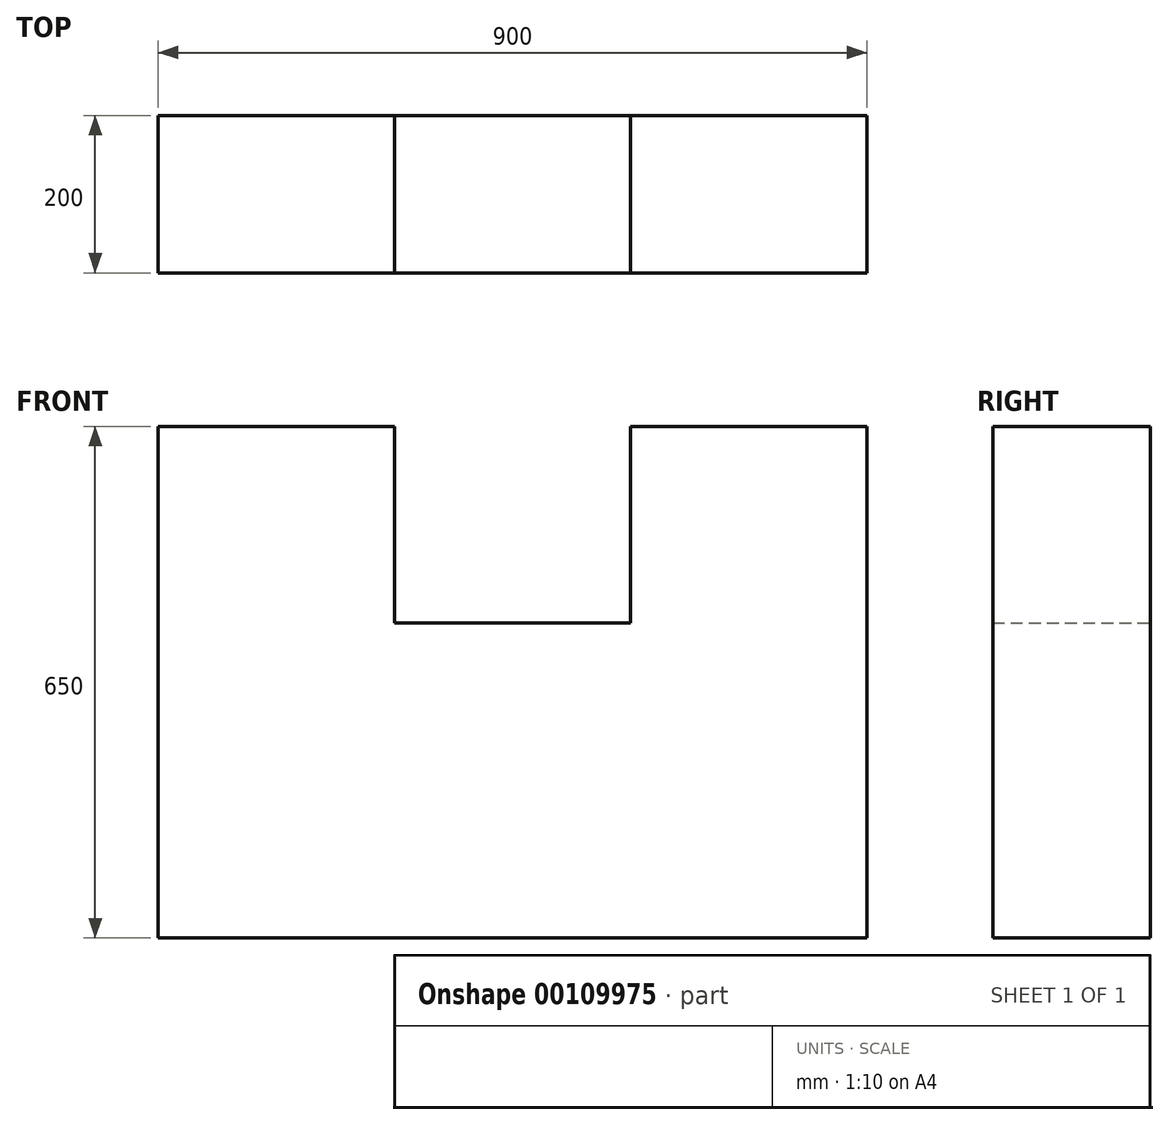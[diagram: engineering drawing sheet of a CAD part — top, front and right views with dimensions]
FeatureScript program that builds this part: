
annotation { "Feature Type Name" : "Feature", "Feature Type Description" : "" }
export const myFeature = defineFeature(function(context is Context, id is Id, definition is map)
    precondition{}
    {
        {
            var Q0;
            Q0=qCreatedBy(makeId("Front.planeOp"),FACE);
            var sketch = newSketch(context, id + "F0", { "sketchPlane" : qUnion([Q0])});
            skLineSegment(sketch, "E0.bottom", {"start": v(450, -325) * mm, "end": v(-450, -325) * mm});
            skLineSegment(sketch, "E0.top", {"start": v(450, 325) * mm, "end": v(-450, 325) * mm});
            skLineSegment(sketch, "E0.left", {"start": v(450, -325) * mm, "end": v(450, 325) * mm});
            skLineSegment(sketch, "E0.right", {"start": v(-450, -325) * mm, "end": v(-450, 325) * mm});
            skPoint(sketch, "E0.middle", {"position": v(0, 0) * mm});
            skLineSegment(sketch, "E1.bottom", {"start": v(150, 75) * mm, "end": v(-150, 75) * mm});
            skLineSegment(sketch, "E1.top", {"start": v(150, 575) * mm, "end": v(-150, 575) * mm});
            skLineSegment(sketch, "E1.left", {"start": v(150, 75) * mm, "end": v(150, 575) * mm});
            skLineSegment(sketch, "E1.right", {"start": v(-150, 75) * mm, "end": v(-150, 575) * mm});
            skPoint(sketch, "E1.middle", {"position": v(0, 325) * mm});
            skSolve(sketch);
        }
        {
            var Q0;
            Q0=makeQuery(id+"F0.imprint","IMPRINT",FACE,{"disambiguationData":[TD([[makeQuery(id+"F0.imprint","IMPRINT",EDGE,{"derivedFrom":sQuery(id+"F0.wireOp",EDGE,"E0.bottom")}),-1.0]])]});
            extrude(context, id + "F1", {"entities" : qUnion([Q0]), "depth" : 200 * mm, "offsetDistance" : 25 * mm});
        }
    });
